# Revit family: Haworth_Eddy_Table_EU_PRELIMINARY
name_source: partatom
category: Furniture Systems
revit_build: Autodesk Revit 2018 (Build: 20170223_1515(x64)
units: mm (PartAtom-declared; Revit-internal decimal feet)

## family parameters
Always vertical = Yes
Cut with Voids When Loaded = No
OmniClass Number = 23.40.70.14.64.21
OmniClass Title = Systems Furniture
Part Type = Normal
Room Calculation Point = No
Round Connector Dimension = Use Diameter
Shared = No
Work Plane-Based = No

## types (2) — shared parameters
Actual Depth = 52 cm
Actual Width = 95 cm
Assembly Code = E2020200
Description = Haworth - Mobile Table - Eddy
Leg Finish = Haworth _ Paint _ Gray Tone
Leg Offset = 10 cm
Manufacturer = Haworth
Model = EYTA0905
Revision Number = 1
Size = Verify Final Dim. w/ Haworth
Table Finish = Haworth _ Polymer _ Snow
Top Thickness = 2 cm
URL = https://www.haworth.com
URL - Product = https://www.haworth.com
Warranty = http://www.haworth.com

## per-type parameters (varying)
| type | Actual Height | Adjustable | Fixed |
| Adjustable Height | 102 cm | Yes | No |
| Fixed Height | 73 cm | No | Yes |

## geometry (parser evidence)
native form markers: Sweep x3
no freeform markers — native parametric forms only
